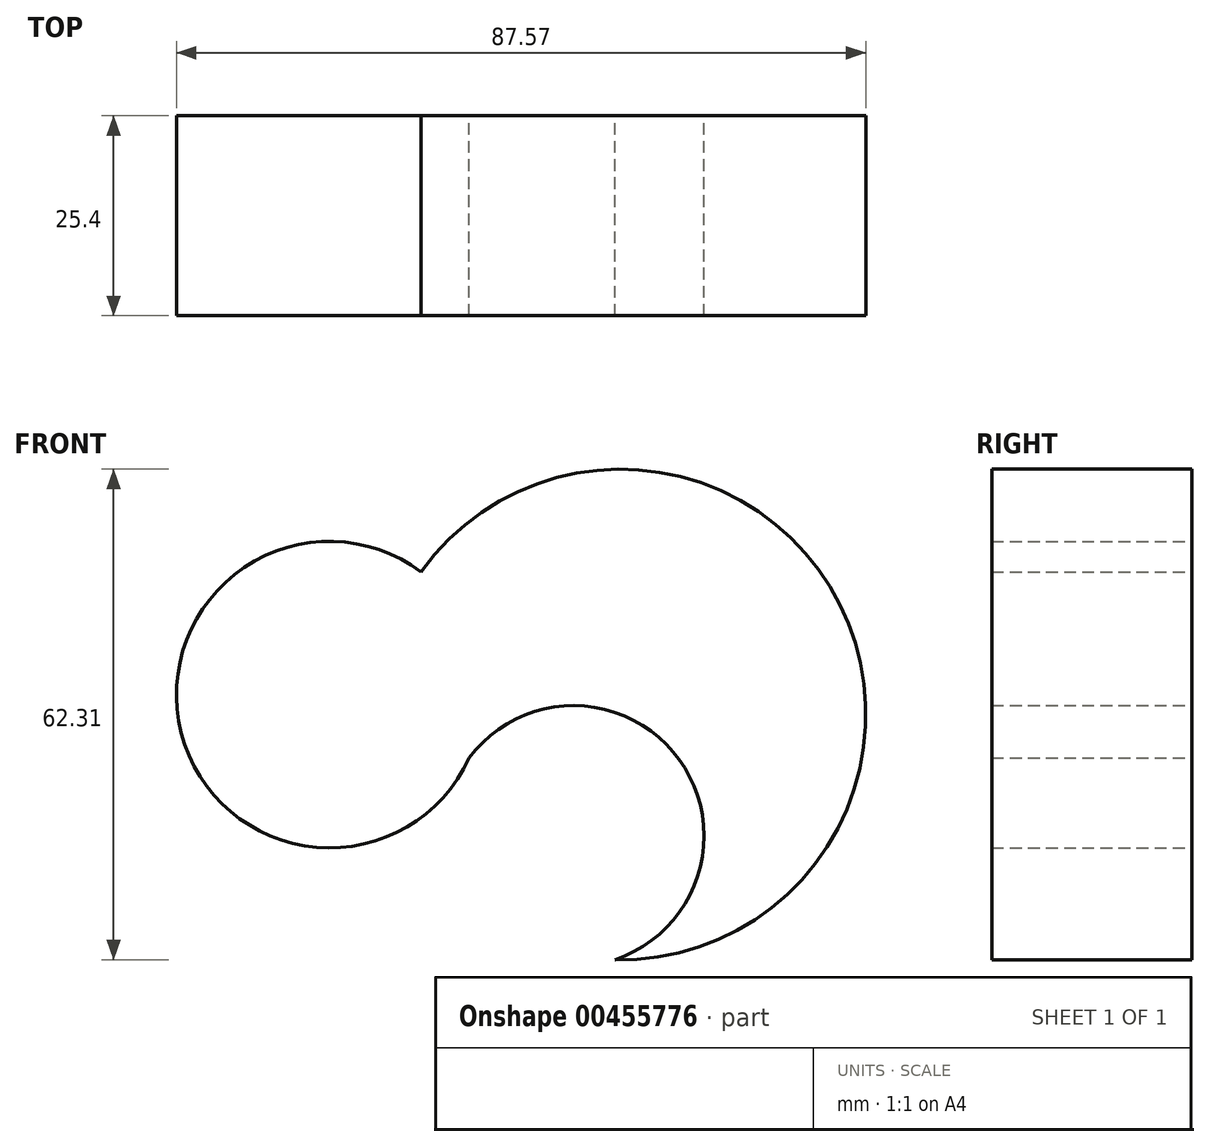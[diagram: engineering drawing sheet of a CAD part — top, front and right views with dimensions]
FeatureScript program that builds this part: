
annotation { "Feature Type Name" : "Feature", "Feature Type Description" : "" }
export const myFeature = defineFeature(function(context is Context, id is Id, definition is map)
    precondition{}
    {
        {
            var Q0;
            Q0=qCreatedBy(makeId("Front.planeOp"),FACE);
            var sketch = newSketch(context, id + "F0", { "sketchPlane" : qUnion([Q0])});
            skArc(sketch, "E0", {"start": v(4.4, 11.95) * mm, "mid": v(32.96, 57.03) * mm, "end": v(-20.25, 61.23) * mm});
            skArc(sketch, "E1", {"start": v(-20.25, 61.23) * mm, "mid": v(-50.71, 40.76) * mm, "end": v(-14.15, 37.57) * mm});
            skArc(sketch, "E2", {"start": v(4.4, 11.95) * mm, "mid": v(12.53, 37.36) * mm, "end": v(-14.15, 37.57) * mm});
            skSolve(sketch);
        }
        {
            var Q0;
            Q0=makeQuery(id+"F0.imprint","IMPRINT",FACE,{"disambiguationData":[TD([[makeQuery(id+"F0.imprint","IMPRINT",EDGE,{"derivedFrom":sQuery(id+"F0.wireOp",EDGE,"E0")}),1.0]])]});
            extrude(context, id + "F1", {"entities" : qUnion([Q0]), "depth" : 25.4 * mm});
        }
    });
